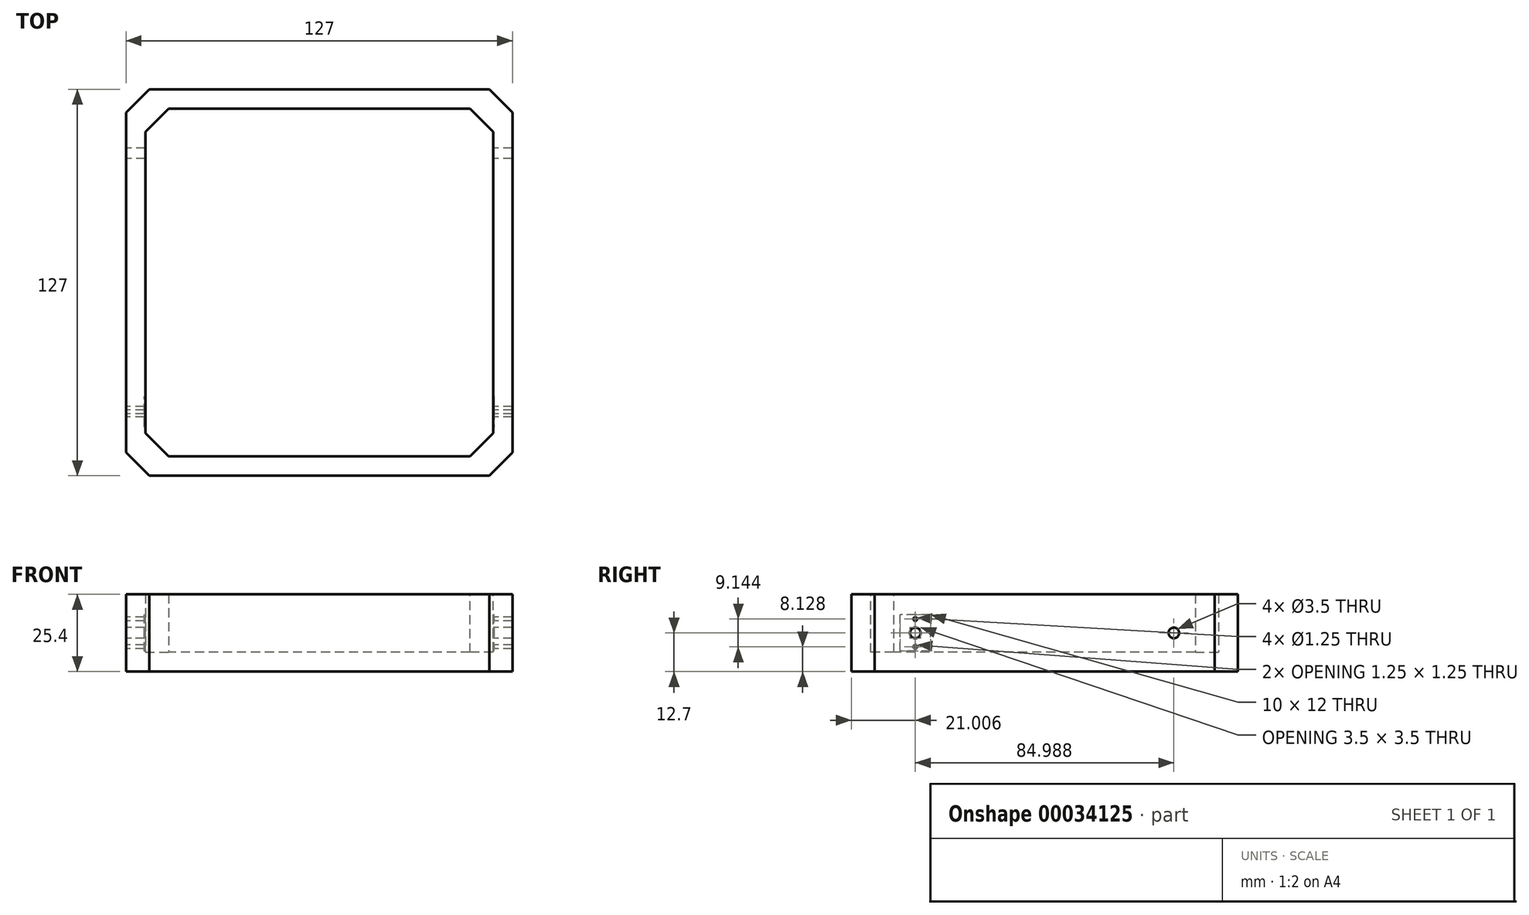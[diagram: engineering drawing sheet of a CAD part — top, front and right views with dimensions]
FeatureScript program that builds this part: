
annotation { "Feature Type Name" : "Feature", "Feature Type Description" : "" }
export const myFeature = defineFeature(function(context is Context, id is Id, definition is map)
    precondition{}
    {
        {
            var Q0;
            Q0=qCreatedBy(makeId("Top.planeOp"),FACE);
            var sketch = newSketch(context, id + "F0", { "sketchPlane" : qUnion([Q0])});
            skLineSegment(sketch, "E0.rect.bottom", {"start": v(63.5, 63.5) * mm, "end": v(-63.5, 63.5) * mm});
            skLineSegment(sketch, "E0.rect.top", {"start": v(63.5, -63.5) * mm, "end": v(-63.5, -63.5) * mm});
            skLineSegment(sketch, "E0.rect.left", {"start": v(63.5, 63.5) * mm, "end": v(63.5, -63.5) * mm});
            skLineSegment(sketch, "E0.rect.right", {"start": v(-63.5, 63.5) * mm, "end": v(-63.5, -63.5) * mm});
            skPoint(sketch, "E0.rect.middle", {"position": v(0, 0) * mm});
            skSolve(sketch);
        }
        {
            var Q0;
            Q0 = qSketchRegion(id + "F0", true);
            extrude(context, id + "F1", {"entities" : qUnion([Q0]), "depth" : 25.4 * mm});
        }
        {
            var Q0;
            Q0=makeQuery(id+"F1.opExtrude","CAP_FACE",FACE,{"disambiguationData":[OSD([sQuery(id+"F0.wireOp",EDGE,"E0.rect.bottom"),sQuery(id+"F0.wireOp",EDGE,"E0.rect.top"),sQuery(id+"F0.wireOp",EDGE,"E0.rect.left"),sQuery(id+"F0.wireOp",EDGE,"E0.rect.right")])],"isStart":false});
            shell(context, id + "F2", {"entities" : qUnion([Q0]), "thickness" : 6.35 * mm});
        }
        {
            var Q0;
            Q0=makeQuery(id+"F1.opExtrude","SWEPT_EDGE",EDGE,{"disambiguationData":[OSD([sQuery(id+"F0.wireOp",EDGE,"E0.rect.top"),sQuery(id+"F0.wireOp",EDGE,"E0.rect.right")])]});
            var Q1;
            Q1=makeQuery(id+"F1.opExtrude","SWEPT_EDGE",EDGE,{"disambiguationData":[OSD([sQuery(id+"F0.wireOp",EDGE,"E0.rect.top"),sQuery(id+"F0.wireOp",EDGE,"E0.rect.left")])]});
            var Q2;
            Q2=makeQuery(id+"F1.opExtrude","SWEPT_EDGE",EDGE,{"disambiguationData":[OSD([sQuery(id+"F0.wireOp",EDGE,"E0.rect.bottom"),sQuery(id+"F0.wireOp",EDGE,"E0.rect.left")])]});
            var Q3;
            Q3=makeQuery(id+"F1.opExtrude","SWEPT_EDGE",EDGE,{"disambiguationData":[OSD([sQuery(id+"F0.wireOp",EDGE,"E0.rect.bottom"),sQuery(id+"F0.wireOp",EDGE,"E0.rect.right")])]});
            var Q4;
            Q4=makeQuery(id+"F2.opShell","OFFSET_EDGE",EDGE,{"disambiguationData":[OSD([sQuery(id+"F0.wireOp",EDGE,"E0.rect.bottom"),sQuery(id+"F0.wireOp",EDGE,"E0.rect.right")])]});
            var Q5;
            Q5=makeQuery(id+"F2.opShell","OFFSET_EDGE",EDGE,{"disambiguationData":[OSD([sQuery(id+"F0.wireOp",EDGE,"E0.rect.bottom"),sQuery(id+"F0.wireOp",EDGE,"E0.rect.left")])]});
            var Q6;
            Q6=makeQuery(id+"F2.opShell","OFFSET_EDGE",EDGE,{"disambiguationData":[OSD([sQuery(id+"F0.wireOp",EDGE,"E0.rect.top"),sQuery(id+"F0.wireOp",EDGE,"E0.rect.left")])]});
            var Q7;
            Q7=makeQuery(id+"F2.opShell","OFFSET_EDGE",EDGE,{"disambiguationData":[OSD([sQuery(id+"F0.wireOp",EDGE,"E0.rect.top"),sQuery(id+"F0.wireOp",EDGE,"E0.rect.right")])]});
            chamfer(context, id + "F3", {"entities" : qUnion([Q0, Q1, Q2, Q3, Q4, Q5, Q6, Q7]), "width" : 7.62 * mm, "tangentPropagation" : true});
        }
        {
            var Q0;
            Q0=makeQuery(id+"F1.opExtrude","SWEPT_FACE",FACE,{"disambiguationData":[OSD([sQuery(id+"F0.wireOp",EDGE,"E0.rect.right")])]});
            var sketch = newSketch(context, id + "F4", { "sketchPlane" : qUnion([Q0])});
            skLineSegment(sketch, "E1", {"start": v(0, 0) * mm, "end": v(0, 25.4) * mm});
            skLineSegment(sketch, "E2.0", {"start": v(42.5, 0) * mm, "end": v(42.5, 25.4) * mm});
            skLineSegment(sketch, "E3.0", {"start": v(-38.1, 0) * mm, "end": v(-38.1, 25.4) * mm});
            skCircle(sketch, "E4", {"center": v(42.5, 12.7) * mm, "radius": 1.75 * mm});
            skLineSegment(sketch, "E5", {"start": v(42.5, 12.7) * mm, "end": v(52.96, 12.7) * mm});
            skPoint(sketch, "E5.endSnap0", {"position": v(55.88, 12.7) * mm});
            skCircle(sketch, "E6", {"center": v(42.5, 17.27) * mm, "radius": 0.62 * mm});
            skCircle(sketch, "E7", {"center": v(42.5, 8.13) * mm, "radius": 0.62 * mm});
            skSolve(sketch);
        }
        {
            var Q0;
            Q0 = qSketchRegion(id + "F4", true);
            extrude(context, id + "F5", {"entities" : qUnion([Q0]), "operationType" : NewBodyOperationType.REMOVE, "endBound" : BoundingType.THROUGH_ALL, "oppositeDirection" : true, "depth" : 25.4 * mm});
        }
        {
            var Q0;
            Q0=makeQuery(id+"F2.opShell","OFFSET_FACE",FACE,{"disambiguationData":[OSD([sQuery(id+"F0.wireOp",EDGE,"E0.rect.right")])]});
            var sketch = newSketch(context, id + "F6", { "sketchPlane" : qUnion([Q0])});
            skLineSegment(sketch, "E8.rect.bottom", {"start": v(-47.5, 6.7) * mm, "end": v(-37.5, 6.7) * mm});
            skLineSegment(sketch, "E8.rect.top", {"start": v(-47.5, 18.7) * mm, "end": v(-37.5, 18.7) * mm});
            skLineSegment(sketch, "E8.rect.left", {"start": v(-47.5, 6.7) * mm, "end": v(-47.5, 18.7) * mm});
            skLineSegment(sketch, "E8.rect.right", {"start": v(-37.5, 6.7) * mm, "end": v(-37.5, 18.7) * mm});
            skPoint(sketch, "E8.rect.middle", {"position": v(-42.5, 12.7) * mm});
            skSolve(sketch);
        }
        {
            var Q0;
            Q0 = qSketchRegion(id + "F6", true);
            extrude(context, id + "F7", {"entities" : qUnion([Q0]), "operationType" : NewBodyOperationType.REMOVE, "oppositeDirection" : true, "depth" : 0.32 * mm});
        }
        {
            var Q0;
            Q0=makeQuery(id+"F2.opShell","OFFSET_FACE",FACE,{"disambiguationData":[OSD([sQuery(id+"F0.wireOp",EDGE,"E0.rect.left")])]});
            var sketch = newSketch(context, id + "F8", { "sketchPlane" : qUnion([Q0])});
            skLineSegment(sketch, "E9.rect.bottom", {"start": v(37.5, 6.7) * mm, "end": v(47.5, 6.7) * mm});
            skLineSegment(sketch, "E9.rect.top", {"start": v(37.5, 18.7) * mm, "end": v(47.5, 18.7) * mm});
            skLineSegment(sketch, "E9.rect.left", {"start": v(37.5, 6.7) * mm, "end": v(37.5, 18.7) * mm});
            skLineSegment(sketch, "E9.rect.right", {"start": v(47.5, 6.7) * mm, "end": v(47.5, 18.7) * mm});
            skPoint(sketch, "E9.rect.middle", {"position": v(42.5, 12.7) * mm});
            skSolve(sketch);
        }
        {
            var Q0;
            Q0 = qSketchRegion(id + "F8", true);
            extrude(context, id + "F9", {"entities" : qUnion([Q0]), "operationType" : NewBodyOperationType.REMOVE, "oppositeDirection" : true, "depth" : 0.32 * mm});
        }
        {
            var Q0;
            Q0=makeQuery(id+"F1.opExtrude","SWEPT_FACE",FACE,{"disambiguationData":[OSD([sQuery(id+"F0.wireOp",EDGE,"E0.rect.right")])]});
            var sketch = newSketch(context, id + "F10", { "sketchPlane" : qUnion([Q0])});
            skLineSegment(sketch, "E10", {"start": v(0, 0) * mm, "end": v(0, 25.4) * mm});
            skLineSegment(sketch, "E11.0", {"start": v(42.5, 0) * mm, "end": v(42.5, 25.4) * mm});
            skLineSegment(sketch, "E12.0", {"start": v(-42.5, 0) * mm, "end": v(-42.5, 25.4) * mm});
            skCircle(sketch, "E13", {"center": v(-42.5, 12.7) * mm, "radius": 1.75 * mm});
            skSolve(sketch);
        }
        {
            var Q0;
            Q0 = qSketchRegion(id + "F10", true);
            extrude(context, id + "F11", {"entities" : qUnion([Q0]), "operationType" : NewBodyOperationType.REMOVE, "endBound" : BoundingType.THROUGH_ALL, "oppositeDirection" : true, "depth" : 25.4 * mm});
        }
    });
